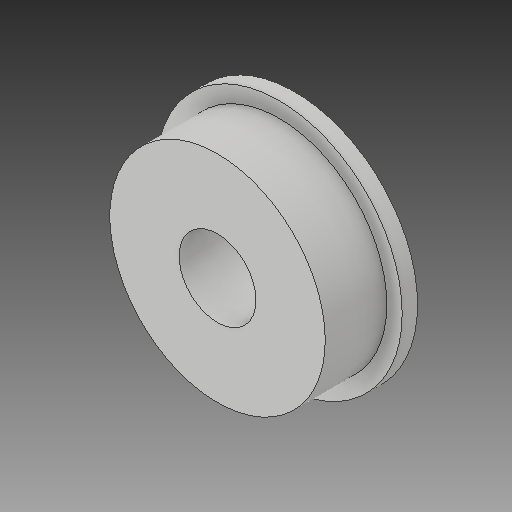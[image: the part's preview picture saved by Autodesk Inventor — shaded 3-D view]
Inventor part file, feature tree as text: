
AUTODESK INVENTOR PART (.ipt)
format: ipt  version: 2018 (Build 220112000, 112)  size: 132,608 bytes
history: native  units: mm
features: other x3, sketch x3
ambient origin geometry x8: Origin, YZ Plane, XZ Plane, XY Plane, X Axis, Y Axis, Z Axis, Center Point
bodies: Solid1 (feature_tree)
feature tree (6):
  other  "Flanged Bearing_CPY.ipt"
  other  "Solid1::Flanged Bearing_CPY.ipt"
  other  "TaggingFeature1"
  sketch  "Sketch1"  dims[d0=10.0mm]
  sketch  "Sketch2"
  sketch  "Sketch3"
